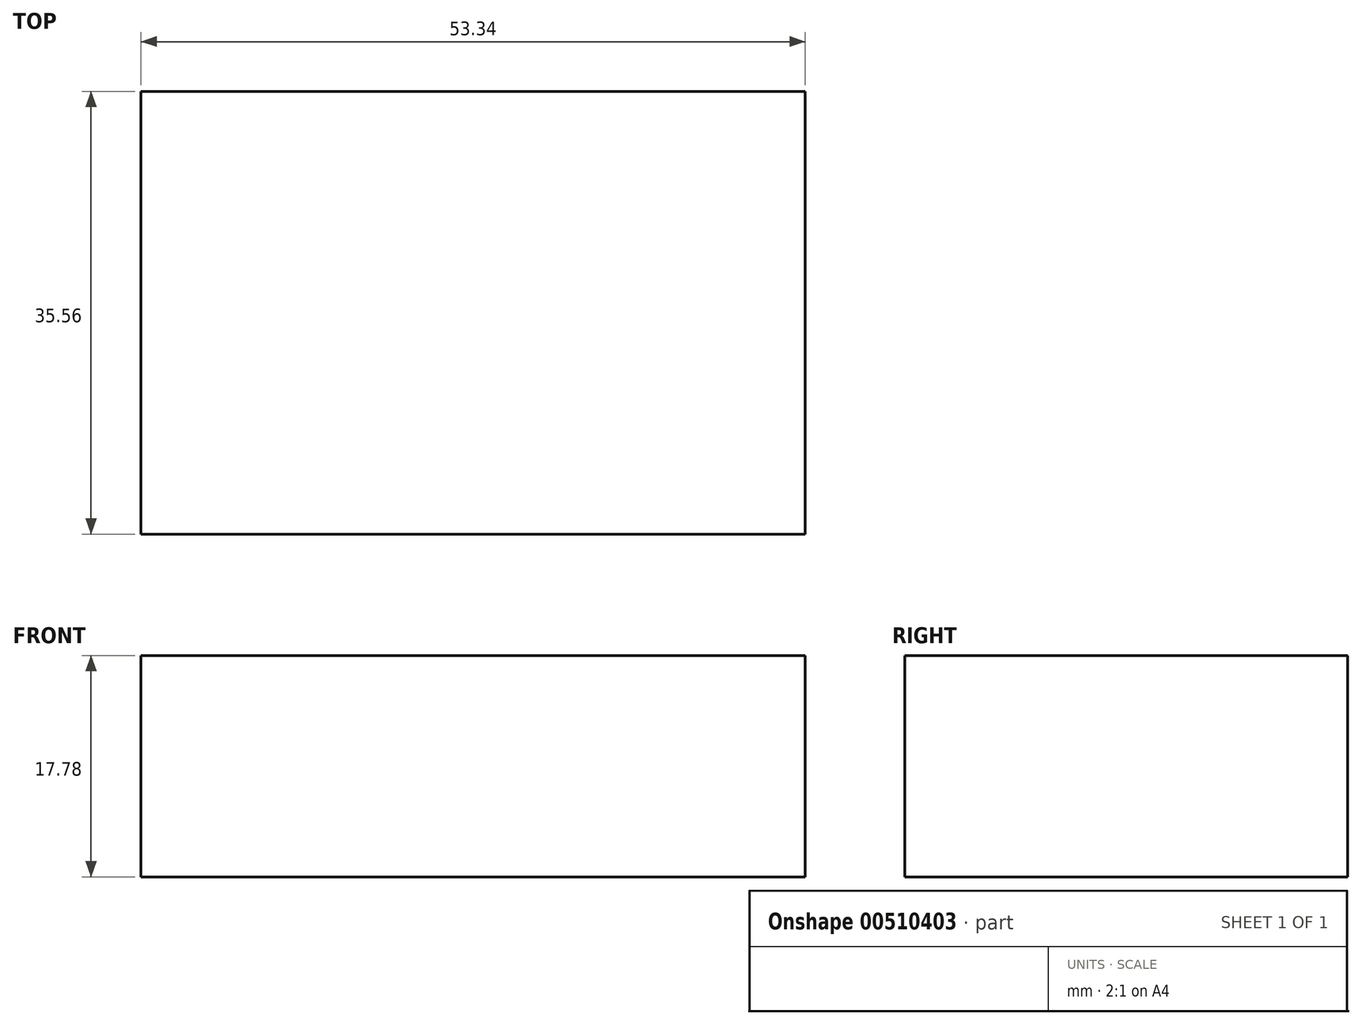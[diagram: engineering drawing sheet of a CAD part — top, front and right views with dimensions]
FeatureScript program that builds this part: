
annotation { "Feature Type Name" : "Feature", "Feature Type Description" : "" }
export const myFeature = defineFeature(function(context is Context, id is Id, definition is map)
    precondition{}
    {
        {
            var Q0;
            Q0=qCreatedBy(makeId("Top.planeOp"),FACE);
            var sketch = newSketch(context, id + "F0", { "sketchPlane" : qUnion([Q0])});
            skLineSegment(sketch, "E0.bottom", {"start": v(0, 0) * mm, "end": v(53.34, 0) * mm});
            skLineSegment(sketch, "E0.top", {"start": v(0, -35.56) * mm, "end": v(53.34, -35.56) * mm});
            skLineSegment(sketch, "E0.left", {"start": v(0, 0) * mm, "end": v(0, -35.56) * mm});
            skLineSegment(sketch, "E0.right", {"start": v(53.34, 0) * mm, "end": v(53.34, -35.56) * mm});
            skSolve(sketch);
        }
        {
            var Q0;
            Q0 = qSketchRegion(id + "F0", true);
            extrude(context, id + "F1", {"entities" : qUnion([Q0]), "depth" : 17.78 * mm});
        }
    });
